# Revit family: Ball_Valves-Full_Port-WATTS-LFFBV3CQC_Series
name_source: partatom
category: Pipe Accessories
revit_build: Autodesk Revit 2014 (Build: 20130308_1515(x64)
units: mm (PartAtom-declared; Revit-internal decimal feet)

## types (3) — shared parameters
Connection Type = Quick Connect
Country = United States
Description = 2 Piece, Full Port, Lead Free Brass Ball Valve
Manufacturer = WATTS
Manufacturer Product Line = Water Safety & Flow Control
Material = Lead Free-WATTS-Copper Silicon Alloy
Max. Working Pressure = 200psi @ 180°F (13.8 bar @ 82°C)
Model = LFFBV-3C-QC
Product Documentation Link = http://media.wattswater.com
Product Page URL = http://www.watts.com
Quick Connect Fillet = 0.09 "
Region = North America
URL = www.watts.com

## per-type parameters (varying)
| type | Annotation Circle Radius | Body Inlet Length | Body Midpoint | Body Outlet Length | Body Radius | Center To Handle Angle | Center To Handle Back | Center To Handle Tang | Center To Inlet | Center To Outlet | Connection Radius | Handle Height | Handle Length | Handle Thickness | Handle Width | Length | Ordering Code | Quick Connect Radius | Stem Height | Stem Radius |
| LFFBV-3C-QC - 0.5" | 0.28 " | 0.46 " | 1.907 " | 0.69 " | 0.56 " | 0.492 " | 0.275 " | 0.436 " | 1.907 " | 1.907 " | 0" | 0.5 " | 3.375 " | 0.098 " | 0.55 " | 3.813 " | 0555269 | 0.515 " | 1.123 " | 0.31 " |
| LFFBV-3C-QC - 0.75" | 0.39 " | 0.63 " | 2.282 " | 0.83 " | 0.78 " | 0.483 " | 0.345 " | 0.53 " | 2.282 " | 2.282 " | 0" | 0.689 " | 4 " | 0.11 " | 0.689 " | 4.563 " | 0555270 | 0.66 " | 1.359 " | 0.375 " |
| LFFBV-3C-QC - 1" | 0.455 " | 0.76 " | 2.5 " | 0.9 " | 0.91 " | 0.577 " | 0.404 " | 0.64 " | 2.5 " | 2.5 " | 1" | 0.75 " | 4.25 " | 0.126 " | 0.807 " | 5 " | 0555271 | 0.79 " | 1.633 " | 0.465 " |

## geometry (parser evidence)
native form markers: Blend x4, Sweep x1
no freeform markers — native parametric forms only
